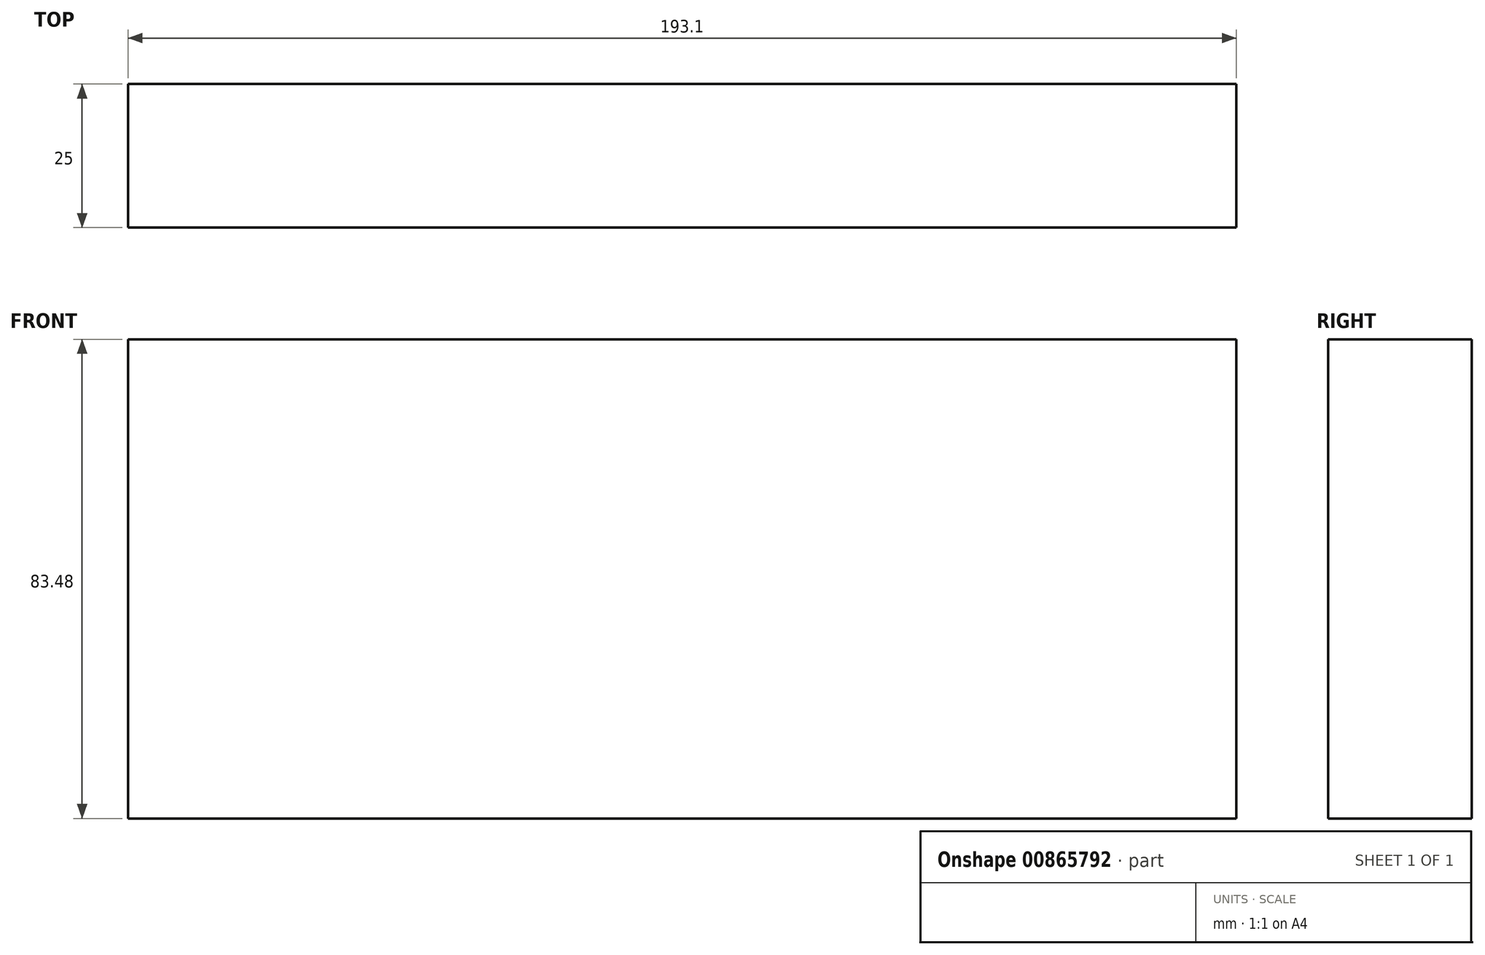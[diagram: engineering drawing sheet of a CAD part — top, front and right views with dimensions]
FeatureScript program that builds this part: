
annotation { "Feature Type Name" : "Feature", "Feature Type Description" : "" }
export const myFeature = defineFeature(function(context is Context, id is Id, definition is map)
    precondition{}
    {
        {
            var Q0;
            Q0=qCreatedBy(makeId("Front.planeOp"),FACE);
            var sketch = newSketch(context, id + "F0", { "sketchPlane" : qUnion([Q0])});
            skLineSegment(sketch, "E0.bottom", {"start": v(-88.68, 38.65) * mm, "end": v(104.42, 38.65) * mm});
            skLineSegment(sketch, "E0.top", {"start": v(-88.68, -44.83) * mm, "end": v(104.42, -44.83) * mm});
            skLineSegment(sketch, "E0.left", {"start": v(-88.68, 38.65) * mm, "end": v(-88.68, -44.83) * mm});
            skLineSegment(sketch, "E0.right", {"start": v(104.42, 38.65) * mm, "end": v(104.42, -44.83) * mm});
            skSolve(sketch);
        }
        {
            var Q0;
            Q0 = qSketchRegion(id + "F0", true);
            extrude(context, id + "F1", {"entities" : qUnion([Q0]), "depth" : 25 * mm, "offsetDistance" : 25 * mm});
        }
    });
